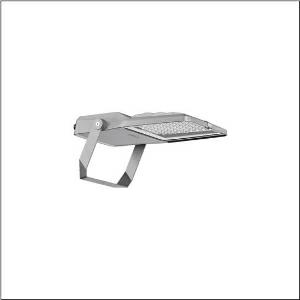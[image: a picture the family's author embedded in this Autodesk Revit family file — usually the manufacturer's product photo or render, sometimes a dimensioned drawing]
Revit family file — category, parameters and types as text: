
# Revit family: floodlight_fl_21_iq_mini___pl64_5xa7772b1e1a_f8ab
name_source: partatom
category: Lighting Fixtures
units: mm (PartAtom-declared; Revit-internal decimal feet)

## family parameters
Cut with Voids When Loaded = No
Host = Face
Light Source = No
Part Type = Normal
Room Calculation Point = No
Round Connector Dimension = Use Diameter
Shared = No

## types (1)
- --- (1 x LED, 4990 lm, 45.5 W, 2200K)
    Apparent Load = 46 VA
    CIE Flux Codes = 28 80 98 100 100
    Color Rendering = 70
    Color Temperature = 2200K
    Default Elevation = 1800 mm
    Description = Floodlight FL 21 iQ mini, floodlight, primary light control with lens, of PMMA, primary optical cover: protective disc, of toughened safety glass, transparent, light distribution: PL64, light emission: direct distribution, installation type: surface-mounted, LED, High Power LED, rated luminous flux: 4.990lm, luminous efficacy: 110lm/W, light colour: 722, colour temperature: 2200K, control gear: iQ Street-Remote/DALI, control: Street-Remote, Auto-Match, Temp-Guard, Night-Set, Smart-Wire, Desk-Remote (wireless, voltage-free reading and setting of iQ features in the workshop via application-optimized NFC function/RFID function), optimised constant luminous flux control (CLO 2.0), with terminal, 6-pole, mains connection: 220..240V, AC, 50/60Hz, start of lifetime: 46W, end of service life: 48W, reduction: 21W, luminaire housing, of diecast aluminium, powder-coated, Siteco® metallic grey (DB 702S), corrosivity category C5 mid according to DIN EN ISO 12944, suitable for swimming pools, chlorine-resistant, sealing non-destructively replaceable, mounting bracket, of steel, galvanised, powder-coated, Siteco® metallic grey (DB 702S), protection rating (complete): IP66, insulation class (complete): insulation class II (safety insulation), certification: CE, ENEC, VDE, protection symbol: D, impact resistance: IK08, permissible operating ambient temperature: -40..+40°C, permissible operating ambient temperature for outdoor applications: -40..+50°C, standard: DIN EN 12944, LABS conformity tested according to VDMA 24364:2018-05, packaging unit: 1 piece

Light Distribution: PL64
    Height = 70 mm
    Lamp = 1 x LED
    Lamp Light Flux = 4990 lm
    Lamp Power = 45.5 W
    Lamp count = 1
    Length = 485 mm
    Luminous efficacy = 110 lm/W
    Manufacturer = Siteco
    ModVariant = No
    Model = 5XA7772B1E1A
    Number of Poles = 1
    OnlyDefault = Yes
    Power Factor = 1
    Product Name = Floodlight FL 21 iQ mini | PL64
    Product group = floodlight | pylon annexe
    ProductGroupID = 6200
    Protection Class = Protection class II
    Protection Degree = IP 66
    RLX_Detail_Level = 1
    RLX_Emergency_Light_Flux = 0 lm
    RLX_Emergency_Type = 0
    RLX_Emergency_Type_DB = No
    RlxData = <blob elided: 96257 chars, md5=cc06ca11>
    Socket = socket
    Standby Power = 0 W
    System Light Flux = 4990 lm
    System Power = 46 W
    Type Comments = factory setting: luminous flux: 100 % | dim-lin: 254 | 463 mA
    Type Image = l_1006845.jpg
    URL = http://relux.com
    VarID = @adj_167010
    Voltage = 0 V
    Weight = 0.00 kg
    Width = 337 mm

## geometry (parser evidence)
native form markers: Blend x4, Sweep x10
no freeform markers — native parametric forms only
